# Revit family: NBS_PineappleContracts_DmstcChrs_RynoClubChair
name_source: partatom
category: Furniture
revit_build: Autodesk Revit 2018 (Build: 20190510_1515(x64)
units: mm (PartAtom-declared; Revit-internal decimal feet)

## family parameters
Always vertical = Yes
Cut with Voids When Loaded = No
Room Calculation Point = No
Shared = No
Work Plane-Based = No

## types (1)
- RynoClubChair
    AssetType = Fixed
    BIMObjectName = NBS_PineappleContracts_DomesticChairs_RynoClubChair
    Category = Pr_40_50_12_22:Dining chairs
    ChairMaterial = NBS_PineappleContracts_IconPurple
    CodePerformance = BS EN 16139: 2013 level 2, BS 5852:2006, UL94 HB flammability standards
    Color = Blaze orange, epic blue, icon purple, vegas yellow, cool green, black, thunder grey, moonwalk grey, lime green, granite
    Depth = 615 mm  [stored 2.01772 ft]
    Description = Ryno club chair
    DurationUnit = year
    Features = Sloping arms to minimise ligature risks, weatherproof, fire retardant, floor fixing option available
    Height = 895 mm  [stored 2.93635 ft]
    HighestSeatingHeight = 450 mm
    IfcExportAs = IfcFurnitureType
    IfcExportType = CHAIR
    IsBuiltIn = No
    LowestSeatingHeight = 450 mm
    ManufacturerName = Pineapple Contracts
    ManufacturerURL = www.pineapplecontracts.com
    Material = UV stabilised polyethylene with anti-microbial additive
    ModelNumber = 1RYCLC-FF-50
    ModelReference = RynoClubChair
    NBSCertification = www.nationalbimlibrary.com/cert/acziaqrm
    NBSDescription = Domestic chairs
    NBSReference = 45-35-20/365
    Name = DomesticChairs_RynoClubChair_PineappleContracts
    NominalDepth = 615 mm  [stored 2.01772 ft]
    NominalHeight = 895 mm  [stored 2.93635 ft]
    NominalLength = 0 mm  [stored 0 ft]
    NominalWidth = 615 mm  [stored 2.01772 ft]
    ProductInformation = https://uk.pineapplecontracts.com
    SeatingHeight = 450 mm
    Shape = Cube
    Size = 895 x 615 x 615 mm
    Status = UNSET
    Style = Chair
    SustainabilityPerformance = 100% recyclable
    Uniclass2015Code = Pr_40_50_12_22
    Uniclass2015Title = Dining chairs
    Uniclass2015Version = Products v1.15
    Version = 2
    WarrantyDescription = Lifetime guarantee against manufacturing faults
    WarrantyDurationUnit = year
    WeightOptions = 50 kg standard model, 18 kg lightweight model, contact manufacturer for additional weight options
    Width = 615 mm  [stored 2.01772 ft]

note: [stored X ft] marks values corroborated as IEEE doubles in the binary element streams (Revit-internal decimal feet)

## geometry (parser evidence)
native form markers: Sweep x2
no freeform markers — native parametric forms only
